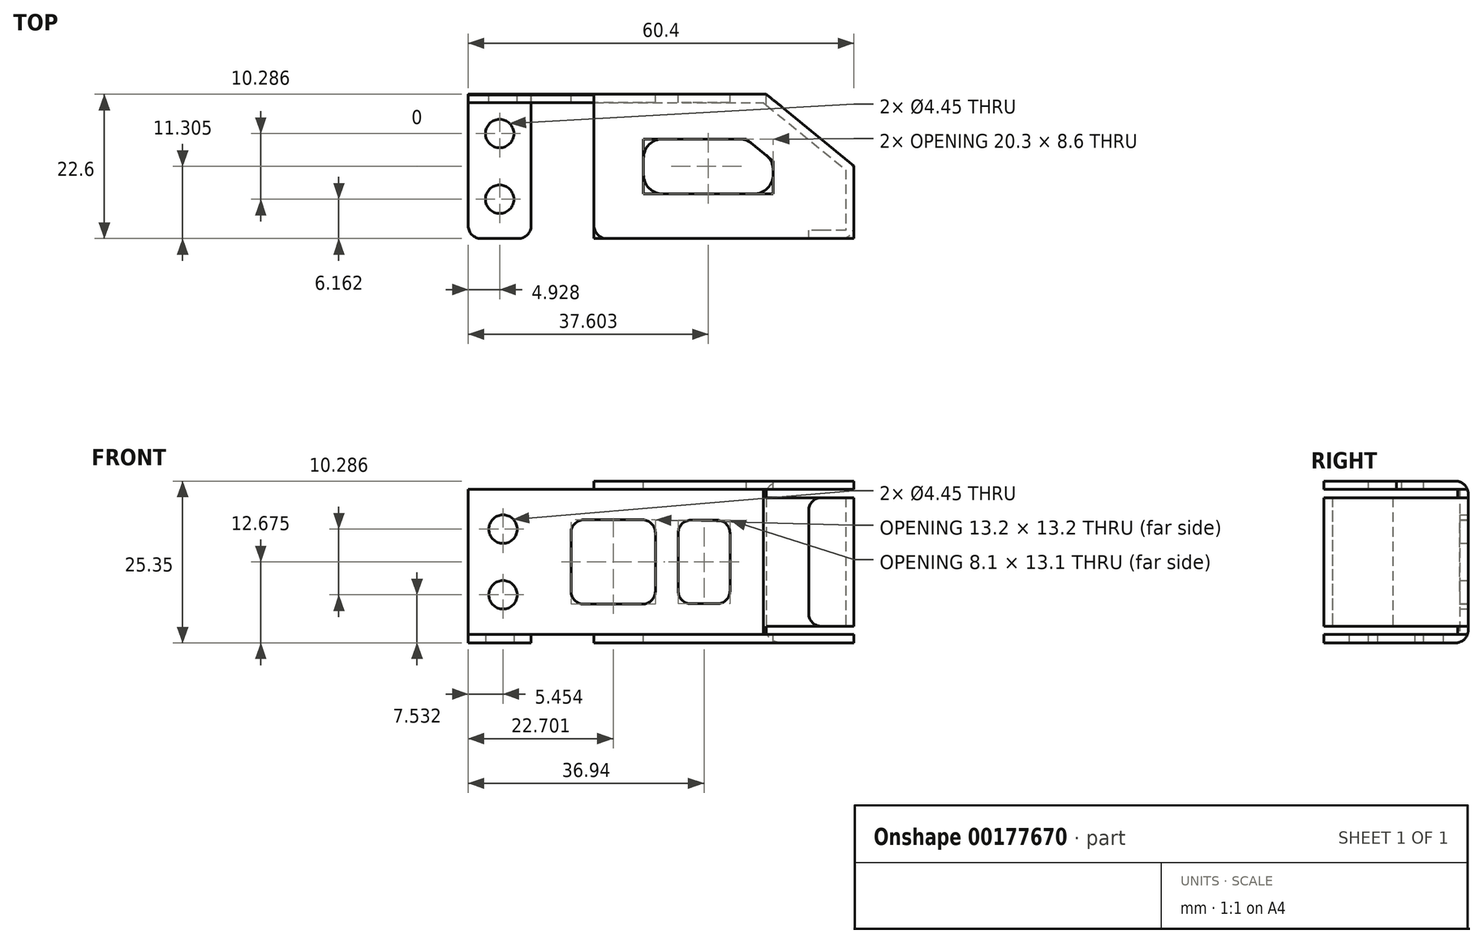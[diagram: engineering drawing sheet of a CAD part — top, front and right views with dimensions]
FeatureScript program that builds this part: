
annotation { "Feature Type Name" : "Feature", "Feature Type Description" : "" }
export const myFeature = defineFeature(function(context is Context, id is Id, definition is map)
    precondition{}
    {
        {
            var Q0;
            Q0=qCreatedBy(makeId("Top.planeOp"),FACE);
            var sketch = newSketch(context, id + "F0", { "sketchPlane" : qUnion([Q0])});
            skLineSegment(sketch, "E0.bottom", {"start": v(-31.59, -12.14) * mm, "end": v(13.31, -12.14) * mm});
            skLineSegment(sketch, "E0.top", {"start": v(-31.59, -33.44) * mm, "end": v(26.21, -33.44) * mm});
            skLineSegment(sketch, "E0.left", {"start": v(-31.59, -12.14) * mm, "end": v(-31.59, -33.44) * mm});
            skLineSegment(sketch, "E0.right", {"start": v(26.21, -22.66) * mm, "end": v(26.21, -33.44) * mm});
            skLineSegment(sketch, "E1", {"start": v(13.31, -12.14) * mm, "end": v(26.21, -22.66) * mm});
            skSolve(sketch);
        }
        {
            var Q0;
            Q0=makeQuery(id+"F0.imprint","IMPRINT",FACE,{"disambiguationData":[TD([[makeQuery(id+"F0.imprint","IMPRINT",EDGE,{"derivedFrom":sQuery(id+"F0.wireOp",EDGE,"E0.bottom")}),-1.0]])]});
            extrude(context, id + "F1", {"entities" : qUnion([Q0]), "depth" : 22.75 * mm});
        }
        {
            var Q0;
            Q0=makeQuery(id+"F1.opExtrude","SWEPT_FACE",FACE,{"disambiguationData":[OSD([sQuery(id+"F0.wireOp",EDGE,"E0.top")])]});
            shell(context, id + "F2", {"entities" : qUnion([Q0]), "thickness" : 1.3 * mm, "oppositeDirection" : true});
        }
        {
            var Q0;
            Q0=makeQuery(id+"F1.opExtrude","SWEPT_FACE",FACE,{"disambiguationData":[OSD([sQuery(id+"F0.wireOp",EDGE,"E0.left")])]});
            var sketch = newSketch(context, id + "F3", { "sketchPlane" : qUnion([Q0])});
            skLineSegment(sketch, "E2", {"start": v(12.14, -1.3) * mm, "end": v(12.14, 22.75) * mm});
            skLineSegment(sketch, "E3", {"start": v(12.14, 22.75) * mm, "end": v(33.44, 22.75) * mm});
            skSolve(sketch);
        }
        {
            var Q0;
            {var subQ0=sQuery(id+"F3.wireOp",EDGE,"E2");Q0=makeQuery(id+"F3.imprint","IMPRINT",FACE,{"disambiguationData":[TD([[makeQuery(id+"F3.imprint","IMPRINT",EDGE,{"derivedFrom":subQ0}),-1.0]])]});}
            extrude(context, id + "F4", {"entities" : qUnion([Q0]), "operationType" : NewBodyOperationType.REMOVE, "oppositeDirection" : true, "depth" : 19.7 * mm});
        }
        {
            var Q0;
            Q0=makeQuery(id+"F1.opExtrude","CAP_FACE",FACE,{"disambiguationData":[OSD([sQuery(id+"F0.wireOp",EDGE,"E0.bottom"),sQuery(id+"F0.wireOp",EDGE,"E0.top"),sQuery(id+"F0.wireOp",EDGE,"E0.left"),sQuery(id+"F0.wireOp",EDGE,"E0.right"),sQuery(id+"F0.wireOp",EDGE,"E1")])],"isStart":false});
            var sketch = newSketch(context, id + "F5", { "sketchPlane" : qUnion([Q0])});
            skLineSegment(sketch, "E4", {"start": v(-13.19, -12.14) * mm, "end": v(-13.19, -33.44) * mm});
            skLineSegment(sketch, "E5", {"start": v(-23.04, -33.44) * mm, "end": v(-23.04, -12.14) * mm});
            skLineSegment(sketch, "E6", {"start": v(-13.19, -33.44) * mm, "end": v(-32.89, -33.44) * mm});
            skLineSegment(sketch, "E7", {"start": v(-32.89, -33.44) * mm, "end": v(-23.04, -33.44) * mm});
            skLineSegment(sketch, "E8", {"start": v(-23.04, -12.14) * mm, "end": v(-32.89, -12.14) * mm});
            skLineSegment(sketch, "E9", {"start": v(-23.04, -12.14) * mm, "end": v(-23.04, -10.84) * mm});
            skLineSegment(sketch, "E10", {"start": v(-13.19, -12.14) * mm, "end": v(-13.19, -10.84) * mm});
            skSolve(sketch);
        }
        {
            var Q0;
            Q0=makeQuery(id+"F5.imprint","IMPRINT",FACE,{"disambiguationData":[TD([[makeQuery(id+"F5.imprint","IMPRINT",EDGE,{"derivedFrom":sQuery(id+"F5.wireOp",EDGE,"E4")}),-1.0]])]});
            extrude(context, id + "F6", {"entities" : qUnion([Q0]), "operationType" : NewBodyOperationType.REMOVE, "oppositeDirection" : true, "depth" : 1.3 * mm});
        }
        {
            var Q0;
            {var subQ0=sQuery(id+"F0.wireOp",EDGE,"E1");var subQ1=sQuery(id+"F0.wireOp",EDGE,"E0.top");var subQ2=sQuery(id+"F0.wireOp",EDGE,"E0.right");var subQ3=sQuery(id+"F0.wireOp",EDGE,"E0.bottom");Q0=makeQuery(id+"F6.boolean.opBoolean","SPLIT",FACE,{"disambiguationData":[TD([makeQuery(id+"F1.opExtrude","SWEPT_FACE",FACE,{"disambiguationData":[OSD([subQ2])]})])],"derivedFrom":makeQuery(id+"F1.opExtrude","CAP_FACE",FACE,{"disambiguationData":[OSD([subQ3,subQ1,sQuery(id+"F0.wireOp",EDGE,"E0.left"),subQ2,subQ0])],"isStart":false})});}
            var sketch = newSketch(context, id + "F7", { "sketchPlane" : qUnion([Q0])});
            skLineSegment(sketch, "E11", {"start": v(-5.44, -17.84) * mm, "end": v(10.65, -17.84) * mm});
            skLineSegment(sketch, "E12", {"start": v(10.65, -17.84) * mm, "end": v(14.86, -21.27) * mm});
            skLineSegment(sketch, "E13", {"start": v(14.86, -21.27) * mm, "end": v(14.86, -26.44) * mm});
            skLineSegment(sketch, "E14", {"start": v(14.86, -26.44) * mm, "end": v(-5.44, -26.44) * mm});
            skLineSegment(sketch, "E15", {"start": v(-5.44, -26.44) * mm, "end": v(-5.44, -17.84) * mm});
            skSolve(sketch);
        }
        {
            var Q0;
            Q0=makeQuery(id+"F7.imprint","IMPRINT",FACE,{"disambiguationData":[TD([[makeQuery(id+"F7.imprint","IMPRINT",EDGE,{"derivedFrom":sQuery(id+"F7.wireOp",EDGE,"E11")}),-1.0]])]});
            extrude(context, id + "F8", {"entities" : qUnion([Q0]), "operationType" : NewBodyOperationType.REMOVE, "oppositeDirection" : true, "depth" : 61.35 * mm});
        }
        {
            var Q0;
            Q0=makeQuery(id+"F1.opExtrude","SWEPT_FACE",FACE,{"disambiguationData":[OSD([sQuery(id+"F0.wireOp",EDGE,"E0.bottom")])]});
            var sketch = newSketch(context, id + "F9", { "sketchPlane" : qUnion([Q0])});
            skLineSegment(sketch, "E16.bottom", {"start": v(-8.1, 4.82) * mm, "end": v(0, 4.82) * mm});
            skLineSegment(sketch, "E16.top", {"start": v(-8.1, 17.93) * mm, "end": v(0, 17.93) * mm});
            skLineSegment(sketch, "E16.left", {"start": v(-8.1, 4.82) * mm, "end": v(-8.1, 17.93) * mm});
            skLineSegment(sketch, "E16.right", {"start": v(0, 4.82) * mm, "end": v(0, 17.93) * mm});
            skLineSegment(sketch, "E17.bottom", {"start": v(3.59, 4.77) * mm, "end": v(16.79, 4.77) * mm});
            skLineSegment(sketch, "E17.top", {"start": v(3.59, 17.97) * mm, "end": v(16.79, 17.97) * mm});
            skLineSegment(sketch, "E17.left", {"start": v(3.59, 4.77) * mm, "end": v(3.59, 17.98) * mm});
            skLineSegment(sketch, "E17.right", {"start": v(16.79, 4.77) * mm, "end": v(16.79, 17.97) * mm});
            skLineSegment(sketch, "E18", {"start": v(27.44, -1.3) * mm, "end": v(27.44, 24.05) * mm, "construction": true});
            skLineSegment(sketch, "E19", {"start": v(-13.78, 11.38) * mm, "end": v(32.89, 11.38) * mm, "construction": true});
            skCircle(sketch, "E20", {"center": v(27.44, 16.52) * mm, "radius": 2.23 * mm});
            skCircle(sketch, "E21", {"center": v(27.44, 6.23) * mm, "radius": 2.23 * mm});
            skLineSegment(sketch, "E22", {"start": v(27.44, 14.3) * mm, "end": v(27.44, 11.38) * mm});
            skLineSegment(sketch, "E23", {"start": v(27.44, 11.38) * mm, "end": v(27.44, 8.46) * mm});
            skLineSegment(sketch, "E24", {"start": v(13.19, -1.3) * mm, "end": v(13.19, 0) * mm});
            skLineSegment(sketch, "E25", {"start": v(13.19, 0) * mm, "end": v(32.89, 0) * mm});
            skPoint(sketch, "E26", {"position": v(16.79, 11.37) * mm});
            skPoint(sketch, "E27", {"position": v(0, 11.37) * mm});
            skSolve(sketch);
        }
        {
            var Q0;
            Q0=makeQuery(id+"F9.imprint","IMPRINT",FACE,{"disambiguationData":[TD([[makeQuery(id+"F9.imprint","IMPRINT",EDGE,{"derivedFrom":sQuery(id+"F9.wireOp",EDGE,"E16.bottom")}),1.0]])]});
            var Q1;
            Q1=makeQuery(id+"F9.imprint","IMPRINT",FACE,{"disambiguationData":[TD([[makeQuery(id+"F9.imprint","IMPRINT",EDGE,{"derivedFrom":sQuery(id+"F9.wireOp",EDGE,"E17.bottom")}),1.0]])]});
            var Q2;
            {var subQ0=sQuery(id+"F9.wireOp",EDGE,"E24");Q2=makeQuery(id+"F9.imprint","IMPRINT",FACE,{"disambiguationData":[TD([[makeQuery(id+"F9.imprint","IMPRINT",EDGE,{"derivedFrom":subQ0}),-1.0]])]});}
            var Q3;
            Q3=makeQuery(id+"F9.imprint","IMPRINT",FACE,{"disambiguationData":[TD([[makeQuery(id+"F9.imprint","IMPRINT",EDGE,{"derivedFrom":sQuery(id+"F9.wireOp",EDGE,"E21")}),1.0]])]});
            var Q4;
            Q4=makeQuery(id+"F9.imprint","IMPRINT",FACE,{"disambiguationData":[TD([[makeQuery(id+"F9.imprint","IMPRINT",EDGE,{"derivedFrom":sQuery(id+"F9.wireOp",EDGE,"E20")}),1.0]])]});
            extrude(context, id + "F10", {"entities" : qUnion([Q0, Q1, Q2, Q3, Q4]), "operationType" : NewBodyOperationType.REMOVE, "oppositeDirection" : true, "depth" : 25 * mm});
        }
        {
            var Q0;
            Q0=makeQuery(id+"F2.opShell","OFFSET_FACE",FACE,{"disambiguationData":[OSD([sQuery(id+"F0.wireOp",EDGE,"E0.right")])]});
            var sketch = newSketch(context, id + "F11", { "sketchPlane" : qUnion([Q0])});
            skLineSegment(sketch, "E28", {"start": v(32.14, 22.75) * mm, "end": v(32.14, 0) * mm});
            skSolve(sketch);
        }
        {
            var Q0;
            {var subQ0=sQuery(id+"F11.wireOp",EDGE,"E28");Q0=makeQuery(id+"F11.imprint","IMPRINT",FACE,{"disambiguationData":[TD([[makeQuery(id+"F11.imprint","IMPRINT",EDGE,{"derivedFrom":subQ0}),1.0]])]});}
            extrude(context, id + "F12", {"entities" : qUnion([Q0]), "operationType" : NewBodyOperationType.ADD, "depth" : 5.8 * mm});
        }
        {
            var Q0;
            Q0=makeQuery(id+"F1.opExtrude","SWEPT_FACE",FACE,{"disambiguationData":[OSD([sQuery(id+"F0.wireOp",EDGE,"E0.bottom")])]});
            var sketch = newSketch(context, id + "F13", { "sketchPlane" : qUnion([Q0])});
            skLineSegment(sketch, "E29", {"start": v(-13.78, 0) * mm, "end": v(-36.67, 0) * mm});
            skLineSegment(sketch, "E30", {"start": v(-13.78, 22.75) * mm, "end": v(-38.37, 22.75) * mm});
            skLineSegment(sketch, "E31", {"start": v(-13.78, 1.3) * mm, "end": v(-36.66, 1.3) * mm});
            skLineSegment(sketch, "E32", {"start": v(-13.78, 21.45) * mm, "end": v(-38.37, 21.45) * mm});
            skLineSegment(sketch, "E33", {"start": v(-36.67, 0) * mm, "end": v(-36.66, 1.3) * mm});
            skLineSegment(sketch, "E34", {"start": v(-38.37, 21.45) * mm, "end": v(-38.37, 22.75) * mm});
            skSolve(sketch);
        }
        {
            var Q0;
            {var subQ0=sQuery(id+"F13.wireOp",EDGE,"E29");Q0=makeQuery(id+"F13.imprint","IMPRINT",FACE,{"disambiguationData":[TD([[makeQuery(id+"F13.imprint","IMPRINT",EDGE,{"derivedFrom":subQ0}),-1.0]])]});}
            var Q1;
            {var subQ0=sQuery(id+"F13.wireOp",EDGE,"E30");Q1=makeQuery(id+"F13.imprint","IMPRINT",FACE,{"disambiguationData":[TD([[makeQuery(id+"F13.imprint","IMPRINT",EDGE,{"derivedFrom":subQ0}),1.0]])]});}
            extrude(context, id + "F14", {"entities" : qUnion([Q0, Q1]), "operationType" : NewBodyOperationType.REMOVE, "oppositeDirection" : true, "depth" : 25 * mm});
        }
        {
            var Q0;
            Q0=makeQuery(id+"F4.boolean.opBoolean","COPY",EDGE,{"derivedFrom":makeQuery(id+"F4.opExtrude","CAP_EDGE",EDGE,{"disambiguationData":[OSD([sQuery(id+"F0.wireOp",EDGE,"E0.top"),sQuery(id+"F0.wireOp",EDGE,"E0.left")])],"isStart":false})});
            var Q1;
            {var subQ0=sQuery(id+"F0.wireOp",EDGE,"E0.right");var subQ1=sQuery(id+"F0.wireOp",EDGE,"E0.top");Q1=makeQuery(id+"F14.boolean.opBoolean","SPLIT",EDGE,{"disambiguationData":[TD([makeQuery(id+"F14.opExtrude","SWEPT_FACE",FACE,{"disambiguationData":[OSD([sQuery(id+"F13.wireOp",EDGE,"E31")])]})])],"derivedFrom":makeQuery(id+"F1.opExtrude","SWEPT_EDGE",EDGE,{"disambiguationData":[OSD([subQ1,subQ0])]})});}
            var Q2;
            {var subQ1=sQuery(id+"F0.wireOp",EDGE,"E0.right");var subQ3=sQuery(id+"F0.wireOp",EDGE,"E0.top");Q2=makeQuery(id+"F14.boolean.opBoolean","SPLIT",EDGE,{"disambiguationData":[TD([makeQuery(id+"F14.opExtrude","SWEPT_FACE",FACE,{"disambiguationData":[OSD([sQuery(id+"F13.wireOp",EDGE,"E29")])]})])],"derivedFrom":makeQuery(id+"F1.opExtrude","SWEPT_EDGE",EDGE,{"disambiguationData":[OSD([subQ3,subQ1])]})});}
            var Q3;
            {var subQ1=sQuery(id+"F0.wireOp",EDGE,"E0.right");var subQ3=sQuery(id+"F0.wireOp",EDGE,"E0.top");Q3=makeQuery(id+"F14.boolean.opBoolean","SPLIT",EDGE,{"disambiguationData":[TD([makeQuery(id+"F4.opExtrude","SWEPT_FACE",FACE,{"disambiguationData":[OSD([sQuery(id+"F3.wireOp",EDGE,"E3")])]})])],"derivedFrom":makeQuery(id+"F1.opExtrude","SWEPT_EDGE",EDGE,{"disambiguationData":[OSD([subQ3,subQ1])]})});}
            var Q4;
            Q4=makeQuery(id+"F6.boolean.opBoolean","COPY",EDGE,{"derivedFrom":makeQuery(id+"F6.opExtrude","SWEPT_EDGE",EDGE,{"disambiguationData":[OSD([sQuery(id+"F0.wireOp",EDGE,"E0.top"),sQuery(id+"F5.wireOp",EDGE,"E4"),sQuery(id+"F5.wireOp",EDGE,"E6")])]})});
            var Q5;
            Q5=makeQuery(id+"F1.opExtrude","SWEPT_EDGE",EDGE,{"disambiguationData":[OSD([sQuery(id+"F0.wireOp",EDGE,"E0.top"),sQuery(id+"F0.wireOp",EDGE,"E0.left")])]});
            var Q6;
            Q6=makeQuery(id+"F6.boolean.opBoolean","COPY",EDGE,{"derivedFrom":makeQuery(id+"F6.opExtrude","SWEPT_EDGE",EDGE,{"disambiguationData":[OSD([sQuery(id+"F5.wireOp",EDGE,"E5"),sQuery(id+"F5.wireOp",EDGE,"E6"),sQuery(id+"F5.wireOp",EDGE,"E7")])]})});
            var Q7;
            Q7=makeQuery(id+"F10.boolean.opBoolean","COPY",EDGE,{"derivedFrom":makeQuery(id+"F10.opExtrude","SWEPT_EDGE",EDGE,{"disambiguationData":[OSD([sQuery(id+"F0.wireOp",EDGE,"E0.bottom"),sQuery(id+"F0.wireOp",EDGE,"E0.left"),sQuery(id+"F9.wireOp",EDGE,"E25")])]})});
            var Q8;
            Q8=makeQuery(id+"F14.boolean.opBoolean","INTERSECT",EDGE,{"derivedFrom":[makeQuery(id+"F12.opExtrude","CAP_FACE",FACE,{"disambiguationData":[OSD([sQuery(id+"F0.wireOp",EDGE,"E0.top"),sQuery(id+"F0.wireOp",EDGE,"E0.right"),sQuery(id+"F11.wireOp",EDGE,"E28")])],"isStart":false}),makeQuery(id+"F14.opExtrude","SWEPT_FACE",FACE,{"disambiguationData":[OSD([sQuery(id+"F13.wireOp",EDGE,"E31")])]})]});
            var Q9;
            Q9=makeQuery(id+"F14.boolean.opBoolean","INTERSECT",EDGE,{"derivedFrom":[makeQuery(id+"F12.opExtrude","CAP_FACE",FACE,{"disambiguationData":[OSD([sQuery(id+"F0.wireOp",EDGE,"E0.top"),sQuery(id+"F0.wireOp",EDGE,"E0.right"),sQuery(id+"F11.wireOp",EDGE,"E28")])],"isStart":false}),makeQuery(id+"F14.opExtrude","SWEPT_FACE",FACE,{"disambiguationData":[OSD([sQuery(id+"F13.wireOp",EDGE,"E32")])]})]});
            fillet(context, id + "F15", {"entities" : qUnion([Q0, Q1, Q2, Q3, Q4, Q5, Q6, Q7, Q8, Q9]), "radius" : 2 * mm, "tangentPropagation" : true, "allowEdgeOverflow" : false});
        }
        {
            var Q0;
            {var subQ0=sQuery(id+"F0.wireOp",EDGE,"E1");var subQ1=sQuery(id+"F0.wireOp",EDGE,"E0.right");var subQ2=sQuery(id+"F0.wireOp",EDGE,"E0.left");var subQ3=sQuery(id+"F0.wireOp",EDGE,"E0.top");var subQ4=sQuery(id+"F0.wireOp",EDGE,"E0.bottom");var subQ5=makeQuery(id+"F1.opExtrude","CAP_FACE",FACE,{"disambiguationData":[OSD([subQ4,subQ3,subQ2,subQ1,subQ0])],"isStart":true});var subQ6=sQuery(id+"F7.wireOp",EDGE,"E13");var subQ7=sQuery(id+"F7.wireOp",EDGE,"E12");Q0=makeQuery(id+"F8.boolean.opBoolean","COPY",EDGE,{"disambiguationData":[TD([subQ5])],"derivedFrom":makeQuery(id+"F8.opExtrude","SWEPT_EDGE",EDGE,{"disambiguationData":[OSD([subQ7,subQ6])]})});}
            var Q1;
            {var subQ0=sQuery(id+"F0.wireOp",EDGE,"E1");var subQ1=sQuery(id+"F0.wireOp",EDGE,"E0.right");var subQ2=sQuery(id+"F0.wireOp",EDGE,"E0.left");var subQ3=sQuery(id+"F0.wireOp",EDGE,"E0.top");var subQ4=sQuery(id+"F0.wireOp",EDGE,"E0.bottom");var subQ5=makeQuery(id+"F1.opExtrude","CAP_FACE",FACE,{"disambiguationData":[OSD([subQ4,subQ3,subQ2,subQ1,subQ0])],"isStart":true});var subQ6=sQuery(id+"F7.wireOp",EDGE,"E11");var subQ7=sQuery(id+"F7.wireOp",EDGE,"E12");Q1=makeQuery(id+"F8.boolean.opBoolean","COPY",EDGE,{"disambiguationData":[TD([subQ5])],"derivedFrom":makeQuery(id+"F8.opExtrude","SWEPT_EDGE",EDGE,{"disambiguationData":[OSD([subQ6,subQ7])]})});}
            var Q2;
            {var subQ0=sQuery(id+"F0.wireOp",EDGE,"E1");var subQ1=sQuery(id+"F0.wireOp",EDGE,"E0.right");var subQ2=sQuery(id+"F0.wireOp",EDGE,"E0.left");var subQ3=sQuery(id+"F0.wireOp",EDGE,"E0.top");var subQ4=sQuery(id+"F0.wireOp",EDGE,"E0.bottom");var subQ5=makeQuery(id+"F1.opExtrude","CAP_FACE",FACE,{"disambiguationData":[OSD([subQ4,subQ3,subQ2,subQ1,subQ0])],"isStart":true});var subQ6=sQuery(id+"F7.wireOp",EDGE,"E11");var subQ7=sQuery(id+"F7.wireOp",EDGE,"E15");Q2=makeQuery(id+"F8.boolean.opBoolean","COPY",EDGE,{"disambiguationData":[TD([subQ5])],"derivedFrom":makeQuery(id+"F8.opExtrude","SWEPT_EDGE",EDGE,{"disambiguationData":[OSD([subQ6,subQ7])]})});}
            var Q3;
            {var subQ0=sQuery(id+"F0.wireOp",EDGE,"E1");var subQ1=sQuery(id+"F0.wireOp",EDGE,"E0.right");var subQ2=sQuery(id+"F0.wireOp",EDGE,"E0.left");var subQ3=sQuery(id+"F0.wireOp",EDGE,"E0.top");var subQ4=sQuery(id+"F0.wireOp",EDGE,"E0.bottom");var subQ5=makeQuery(id+"F1.opExtrude","CAP_FACE",FACE,{"disambiguationData":[OSD([subQ4,subQ3,subQ2,subQ1,subQ0])],"isStart":true});var subQ6=sQuery(id+"F7.wireOp",EDGE,"E14");var subQ7=sQuery(id+"F7.wireOp",EDGE,"E15");Q3=makeQuery(id+"F8.boolean.opBoolean","COPY",EDGE,{"disambiguationData":[TD([subQ5])],"derivedFrom":makeQuery(id+"F8.opExtrude","SWEPT_EDGE",EDGE,{"disambiguationData":[OSD([subQ6,subQ7])]})});}
            var Q4;
            {var subQ0=sQuery(id+"F0.wireOp",EDGE,"E1");var subQ1=sQuery(id+"F0.wireOp",EDGE,"E0.right");var subQ2=sQuery(id+"F0.wireOp",EDGE,"E0.left");var subQ3=sQuery(id+"F0.wireOp",EDGE,"E0.top");var subQ4=sQuery(id+"F0.wireOp",EDGE,"E0.bottom");var subQ5=makeQuery(id+"F1.opExtrude","CAP_FACE",FACE,{"disambiguationData":[OSD([subQ4,subQ3,subQ2,subQ1,subQ0])],"isStart":true});var subQ6=sQuery(id+"F7.wireOp",EDGE,"E13");var subQ7=sQuery(id+"F7.wireOp",EDGE,"E14");Q4=makeQuery(id+"F8.boolean.opBoolean","COPY",EDGE,{"disambiguationData":[TD([subQ5])],"derivedFrom":makeQuery(id+"F8.opExtrude","SWEPT_EDGE",EDGE,{"disambiguationData":[OSD([subQ6,subQ7])]})});}
            var Q5;
            {var subQ0=sQuery(id+"F7.wireOp",EDGE,"E11");var subQ7=sQuery(id+"F7.wireOp",EDGE,"E12");Q5=makeQuery(id+"F8.boolean.opBoolean","COPY",EDGE,{"disambiguationData":[TD([makeQuery(id+"F4.opExtrude","SWEPT_FACE",FACE,{"disambiguationData":[OSD([sQuery(id+"F3.wireOp",EDGE,"E3")])]})])],"derivedFrom":makeQuery(id+"F8.opExtrude","SWEPT_EDGE",EDGE,{"disambiguationData":[OSD([subQ0,subQ7])]})});}
            var Q6;
            {var subQ0=sQuery(id+"F7.wireOp",EDGE,"E12");var subQ7=sQuery(id+"F7.wireOp",EDGE,"E13");Q6=makeQuery(id+"F8.boolean.opBoolean","COPY",EDGE,{"disambiguationData":[TD([makeQuery(id+"F4.opExtrude","SWEPT_FACE",FACE,{"disambiguationData":[OSD([sQuery(id+"F3.wireOp",EDGE,"E3")])]})])],"derivedFrom":makeQuery(id+"F8.opExtrude","SWEPT_EDGE",EDGE,{"disambiguationData":[OSD([subQ0,subQ7])]})});}
            var Q7;
            {var subQ0=sQuery(id+"F7.wireOp",EDGE,"E13");var subQ7=sQuery(id+"F7.wireOp",EDGE,"E14");Q7=makeQuery(id+"F8.boolean.opBoolean","COPY",EDGE,{"disambiguationData":[TD([makeQuery(id+"F4.opExtrude","SWEPT_FACE",FACE,{"disambiguationData":[OSD([sQuery(id+"F3.wireOp",EDGE,"E3")])]})])],"derivedFrom":makeQuery(id+"F8.opExtrude","SWEPT_EDGE",EDGE,{"disambiguationData":[OSD([subQ0,subQ7])]})});}
            var Q8;
            {var subQ0=sQuery(id+"F7.wireOp",EDGE,"E14");var subQ7=sQuery(id+"F7.wireOp",EDGE,"E15");Q8=makeQuery(id+"F8.boolean.opBoolean","COPY",EDGE,{"disambiguationData":[TD([makeQuery(id+"F4.opExtrude","SWEPT_FACE",FACE,{"disambiguationData":[OSD([sQuery(id+"F3.wireOp",EDGE,"E3")])]})])],"derivedFrom":makeQuery(id+"F8.opExtrude","SWEPT_EDGE",EDGE,{"disambiguationData":[OSD([subQ0,subQ7])]})});}
            var Q9;
            {var subQ0=sQuery(id+"F7.wireOp",EDGE,"E11");var subQ7=sQuery(id+"F7.wireOp",EDGE,"E15");Q9=makeQuery(id+"F8.boolean.opBoolean","COPY",EDGE,{"disambiguationData":[TD([makeQuery(id+"F4.opExtrude","SWEPT_FACE",FACE,{"disambiguationData":[OSD([sQuery(id+"F3.wireOp",EDGE,"E3")])]})])],"derivedFrom":makeQuery(id+"F8.opExtrude","SWEPT_EDGE",EDGE,{"disambiguationData":[OSD([subQ0,subQ7])]})});}
            fillet(context, id + "F16", {"entities" : qUnion([Q0, Q1, Q2, Q3, Q4, Q5, Q6, Q7, Q8, Q9]), "radius" : 3 * mm, "tangentPropagation" : true, "allowEdgeOverflow" : false});
        }
        {
            var Q0;
            {var subQ0=sQuery(id+"F0.wireOp",EDGE,"E0.bottom");var subQ1=sQuery(id+"F0.wireOp",EDGE,"E1");Q0=makeQuery(id+"F6.boolean.opBoolean","SPLIT",EDGE,{"disambiguationData":[TD([makeQuery(id+"F1.opExtrude","SWEPT_FACE",FACE,{"disambiguationData":[OSD([subQ1])]})])],"derivedFrom":makeQuery(id+"F1.opExtrude","CAP_EDGE",EDGE,{"disambiguationData":[OSD([subQ0])],"isStart":false})});}
            var Q1;
            {var subQ0=sQuery(id+"F0.wireOp",EDGE,"E0.bottom");var subQ1=sQuery(id+"F0.wireOp",EDGE,"E0.left");Q1=makeQuery(id+"F6.boolean.opBoolean","SPLIT",EDGE,{"disambiguationData":[TD([makeQuery(id+"F1.opExtrude","SWEPT_FACE",FACE,{"disambiguationData":[OSD([subQ1])]})])],"derivedFrom":makeQuery(id+"F1.opExtrude","CAP_EDGE",EDGE,{"disambiguationData":[OSD([subQ0])],"isStart":false})});}
            var Q2;
            Q2=makeQuery(id+"F1.opExtrude","CAP_EDGE",EDGE,{"disambiguationData":[OSD([sQuery(id+"F0.wireOp",EDGE,"E0.bottom")])],"isStart":true});
            var Q3;
            {var subQ0=sQuery(id+"F0.wireOp",EDGE,"E0.right");var subQ1=sQuery(id+"F0.wireOp",EDGE,"E1");Q3=makeQuery(id+"F14.boolean.opBoolean","SPLIT",EDGE,{"disambiguationData":[TD([makeQuery(id+"F14.opExtrude","SWEPT_FACE",FACE,{"disambiguationData":[OSD([sQuery(id+"F13.wireOp",EDGE,"E31")])]})])],"derivedFrom":makeQuery(id+"F1.opExtrude","SWEPT_EDGE",EDGE,{"disambiguationData":[OSD([subQ0,subQ1])]})});}
            var Q4;
            {var subQ0=sQuery(id+"F0.wireOp",EDGE,"E1");var subQ1=sQuery(id+"F0.wireOp",EDGE,"E0.right");Q4=makeQuery(id+"F14.boolean.opBoolean","SPLIT",EDGE,{"disambiguationData":[TD([makeQuery(id+"F4.opExtrude","SWEPT_FACE",FACE,{"disambiguationData":[OSD([sQuery(id+"F3.wireOp",EDGE,"E3")])]})])],"derivedFrom":makeQuery(id+"F1.opExtrude","SWEPT_EDGE",EDGE,{"disambiguationData":[OSD([subQ1,subQ0])]})});}
            var Q5;
            {var subQ0=sQuery(id+"F0.wireOp",EDGE,"E1");var subQ1=sQuery(id+"F0.wireOp",EDGE,"E0.right");Q5=makeQuery(id+"F14.boolean.opBoolean","SPLIT",EDGE,{"disambiguationData":[TD([makeQuery(id+"F14.opExtrude","SWEPT_FACE",FACE,{"disambiguationData":[OSD([sQuery(id+"F13.wireOp",EDGE,"E29")])]})])],"derivedFrom":makeQuery(id+"F1.opExtrude","SWEPT_EDGE",EDGE,{"disambiguationData":[OSD([subQ1,subQ0])]})});}
            fillet(context, id + "F17", {"entities" : qUnion([Q0, Q1, Q2, Q3, Q4, Q5]), "radius" : 2 * mm, "tangentPropagation" : true, "allowEdgeOverflow" : false});
        }
        {
            var Q0;
            Q0=makeQuery(id+"F10.boolean.opBoolean","COPY",EDGE,{"derivedFrom":makeQuery(id+"F10.opExtrude","SWEPT_EDGE",EDGE,{"disambiguationData":[OSD([sQuery(id+"F9.wireOp",EDGE,"E16.top"),sQuery(id+"F9.wireOp",EDGE,"E16.right")])]})});
            var Q1;
            Q1=makeQuery(id+"F10.boolean.opBoolean","COPY",EDGE,{"derivedFrom":makeQuery(id+"F10.opExtrude","SWEPT_EDGE",EDGE,{"disambiguationData":[OSD([sQuery(id+"F9.wireOp",EDGE,"E16.bottom"),sQuery(id+"F9.wireOp",EDGE,"E16.right")])]})});
            var Q2;
            Q2=makeQuery(id+"F10.boolean.opBoolean","COPY",EDGE,{"derivedFrom":makeQuery(id+"F10.opExtrude","SWEPT_EDGE",EDGE,{"disambiguationData":[OSD([sQuery(id+"F9.wireOp",EDGE,"E16.bottom"),sQuery(id+"F9.wireOp",EDGE,"E16.left")])]})});
            var Q3;
            Q3=makeQuery(id+"F10.boolean.opBoolean","COPY",EDGE,{"derivedFrom":makeQuery(id+"F10.opExtrude","SWEPT_EDGE",EDGE,{"disambiguationData":[OSD([sQuery(id+"F9.wireOp",EDGE,"E16.top"),sQuery(id+"F9.wireOp",EDGE,"E16.left")])]})});
            var Q4;
            Q4=makeQuery(id+"F10.boolean.opBoolean","COPY",EDGE,{"derivedFrom":makeQuery(id+"F10.opExtrude","SWEPT_EDGE",EDGE,{"disambiguationData":[OSD([sQuery(id+"F9.wireOp",EDGE,"E17.bottom"),sQuery(id+"F9.wireOp",EDGE,"E17.right")])]})});
            var Q5;
            Q5=makeQuery(id+"F10.boolean.opBoolean","COPY",EDGE,{"derivedFrom":makeQuery(id+"F10.opExtrude","SWEPT_EDGE",EDGE,{"disambiguationData":[OSD([sQuery(id+"F9.wireOp",EDGE,"E17.top"),sQuery(id+"F9.wireOp",EDGE,"E17.right")])]})});
            var Q6;
            Q6=makeQuery(id+"F10.boolean.opBoolean","COPY",EDGE,{"derivedFrom":makeQuery(id+"F10.opExtrude","SWEPT_EDGE",EDGE,{"disambiguationData":[OSD([sQuery(id+"F9.wireOp",EDGE,"E17.top"),sQuery(id+"F9.wireOp",EDGE,"E17.left")])]})});
            var Q7;
            Q7=makeQuery(id+"F10.boolean.opBoolean","COPY",EDGE,{"derivedFrom":makeQuery(id+"F10.opExtrude","SWEPT_EDGE",EDGE,{"disambiguationData":[OSD([sQuery(id+"F9.wireOp",EDGE,"E17.bottom"),sQuery(id+"F9.wireOp",EDGE,"E17.left")])]})});
            fillet(context, id + "F18", {"entities" : qUnion([Q0, Q1, Q2, Q3, Q4, Q5, Q6, Q7]), "radius" : 2 * mm, "tangentPropagation" : true, "allowEdgeOverflow" : false});
        }
        {
            var Q0;
            Q0=makeQuery(id+"F1.opExtrude","CAP_FACE",FACE,{"disambiguationData":[OSD([sQuery(id+"F0.wireOp",EDGE,"E0.bottom"),sQuery(id+"F0.wireOp",EDGE,"E0.top"),sQuery(id+"F0.wireOp",EDGE,"E0.left"),sQuery(id+"F0.wireOp",EDGE,"E0.right"),sQuery(id+"F0.wireOp",EDGE,"E1")])],"isStart":true});
            var sketch = newSketch(context, id + "F19", { "sketchPlane" : qUnion([Q0])});
            skLineSegment(sketch, "E35.0", {"start": v(13.78, 10.84) * mm, "end": v(-32.4, 10.84) * mm});
            skLineSegment(sketch, "E36.0", {"start": v(-23.04, 31.44) * mm, "end": v(-23.04, 12.14) * mm});
            skArc(sketch, "E37.0", {"start": v(-23.04, 31.44) * mm, "mid": v(-23.62, 32.85) * mm, "end": v(-25.04, 33.44) * mm});
            skLineSegment(sketch, "E38.0", {"start": v(-30.89, 33.44) * mm, "end": v(-25.04, 33.44) * mm});
            skArc(sketch, "E39.0", {"start": v(-30.89, 33.44) * mm, "mid": v(-32.3, 32.85) * mm, "end": v(-32.89, 31.44) * mm});
            skLineSegment(sketch, "E40.0", {"start": v(-32.89, 12.14) * mm, "end": v(-32.89, 31.44) * mm});
            skLineSegment(sketch, "E41", {"start": v(-23.04, 12.14) * mm, "end": v(-23.04, 10.84) * mm});
            skLineSegment(sketch, "E42", {"start": v(-23.04, 10.84) * mm, "end": v(-32.89, 10.84) * mm});
            skLineSegment(sketch, "E43", {"start": v(-32.89, 10.84) * mm, "end": v(-32.89, 12.14) * mm});
            skSolve(sketch);
        }
        {
            var Q0;
            Q0=qSketchRegion(id+"F19",true);
            extrude(context, id + "F20", {"entities" : qUnion([Q0]), "operationType" : NewBodyOperationType.ADD, "oppositeDirection" : true, "depth" : 1.3 * mm});
        }
        {
            var Q0;
            Q0=makeQuery(id+"F20.opExtrude","CAP_FACE",FACE,{"disambiguationData":[OSD([sQuery(id+"F19.wireOp",EDGE,"E36.0"),sQuery(id+"F19.wireOp",EDGE,"E37.0"),sQuery(id+"F19.wireOp",EDGE,"E38.0"),sQuery(id+"F19.wireOp",EDGE,"E39.0"),sQuery(id+"F19.wireOp",EDGE,"E40.0"),sQuery(id+"F19.wireOp",EDGE,"E41"),sQuery(id+"F19.wireOp",EDGE,"E42"),sQuery(id+"F19.wireOp",EDGE,"E43")])],"isStart":false});
            var sketch = newSketch(context, id + "F21", { "sketchPlane" : qUnion([Q0])});
            skLineSegment(sketch, "E44.0", {"start": v(-32.89, -10.84) * mm, "end": v(-32.89, -12.14) * mm});
            skLineSegment(sketch, "E45.0", {"start": v(-23.04, -12.14) * mm, "end": v(-30.89, -12.14) * mm});
            skLineSegment(sketch, "E46", {"start": v(-30.89, -12.14) * mm, "end": v(-32.89, -12.14) * mm});
            skLineSegment(sketch, "E47", {"start": v(-23.04, -12.14) * mm, "end": v(-23.04, -10.96) * mm});
            skLineSegment(sketch, "E48", {"start": v(-23.04, -10.96) * mm, "end": v(-23.04, -10.84) * mm});
            skLineSegment(sketch, "E49", {"start": v(-23.04, -10.84) * mm, "end": v(-32.89, -10.84) * mm});
            skSolve(sketch);
        }
        {
            var Q0;
            Q0=qSketchRegion(id+"F21",true);
            extrude(context, id + "F22", {"entities" : qUnion([Q0]), "operationType" : NewBodyOperationType.ADD, "depth" : 2.5 * mm});
        }
        {
            var Q0;
            Q0=makeQuery(id+"F20.opExtrude","CAP_EDGE",EDGE,{"disambiguationData":[OSD([sQuery(id+"F19.wireOp",EDGE,"E42")])],"isStart":true});
            fillet(context, id + "F23", {"entities" : qUnion([Q0]), "radius" : 2 * mm, "tangentPropagation" : true, "allowEdgeOverflow" : false});
        }
        {
            var Q0;
            {var subQ0=sQuery(id+"F0.wireOp",EDGE,"E0.bottom");var subQ1=sQuery(id+"F0.wireOp",EDGE,"E0.top");var subQ2=sQuery(id+"F0.wireOp",EDGE,"E0.left");Q0=makeQuery(id+"F6.boolean.opBoolean","SPLIT",FACE,{"disambiguationData":[TD([makeQuery(id+"F1.opExtrude","SWEPT_FACE",FACE,{"disambiguationData":[OSD([subQ2])]})])],"derivedFrom":makeQuery(id+"F1.opExtrude","CAP_FACE",FACE,{"disambiguationData":[OSD([subQ0,subQ1,subQ2,sQuery(id+"F0.wireOp",EDGE,"E0.right"),sQuery(id+"F0.wireOp",EDGE,"E1")])],"isStart":false})});}
            var sketch = newSketch(context, id + "F24", { "sketchPlane" : qUnion([Q0])});
            skLineSegment(sketch, "E50.0", {"start": v(-13.19, -10.96) * mm, "end": v(-13.19, -12.14) * mm});
            skLineSegment(sketch, "E51.0", {"start": v(-32.89, -10.84) * mm, "end": v(-13.19, -10.84) * mm});
            skLineSegment(sketch, "E52.0", {"start": v(-32.89, -12.84) * mm, "end": v(-32.89, -31.44) * mm});
            skLineSegment(sketch, "E53.0", {"start": v(-32.89, -12.84) * mm, "end": v(-32.89, -10.84) * mm});
            skLineSegment(sketch, "E54.0", {"start": v(-13.19, -12.84) * mm, "end": v(-13.19, -10.96) * mm});
            skLineSegment(sketch, "E55.0", {"start": v(-13.19, -12.84) * mm, "end": v(-13.19, -31.44) * mm});
            skLineSegment(sketch, "E56.0", {"start": v(-30.89, -33.44) * mm, "end": v(-25.04, -33.44) * mm});
            skArc(sketch, "E57.0", {"start": v(-32.89, -31.44) * mm, "mid": v(-32.3, -32.85) * mm, "end": v(-30.89, -33.44) * mm});
            skLineSegment(sketch, "E58", {"start": v(-13.19, -33.44) * mm, "end": v(-25.04, -33.44) * mm});
            skLineSegment(sketch, "E59", {"start": v(-13.19, -31.44) * mm, "end": v(-13.19, -33.44) * mm});
            skPoint(sketch, "E60.orphan", {"position": v(-11.19, -33.44) * mm});
            skLineSegment(sketch, "E61", {"start": v(-13.19, -10.96) * mm, "end": v(-13.19, -10.84) * mm});
            skPoint(sketch, "E62.orphan", {"position": v(13.78, -10.84) * mm});
            skSolve(sketch);
        }
        {
            var Q0;
            Q0=qSketchRegion(id+"F24",true);
            extrude(context, id + "F25", {"entities" : qUnion([Q0]), "operationType" : NewBodyOperationType.REMOVE, "oppositeDirection" : true, "depth" : 1.3 * mm});
        }
        {
            var Q0;
            Q0=makeQuery(id+"F20.opExtrude","CAP_FACE",FACE,{"disambiguationData":[OSD([sQuery(id+"F19.wireOp",EDGE,"E36.0"),sQuery(id+"F19.wireOp",EDGE,"E37.0"),sQuery(id+"F19.wireOp",EDGE,"E38.0"),sQuery(id+"F19.wireOp",EDGE,"E39.0"),sQuery(id+"F19.wireOp",EDGE,"E40.0"),sQuery(id+"F19.wireOp",EDGE,"E41"),sQuery(id+"F19.wireOp",EDGE,"E42"),sQuery(id+"F19.wireOp",EDGE,"E43")])],"isStart":true});
            var sketch = newSketch(context, id + "F26", { "sketchPlane" : qUnion([Q0])});
            skLineSegment(sketch, "E63", {"start": v(-23.04, 22.14) * mm, "end": v(-32.89, 22.14) * mm, "construction": true});
            skLineSegment(sketch, "E64", {"start": v(-27.96, 12.84) * mm, "end": v(-27.96, 33.44) * mm, "construction": true});
            skCircle(sketch, "E65", {"center": v(-27.96, 27.28) * mm, "radius": 2.23 * mm});
            skCircle(sketch, "E66", {"center": v(-27.96, 17) * mm, "radius": 2.23 * mm});
            skLineSegment(sketch, "E67", {"start": v(-27.96, 17) * mm, "end": v(-27.96, 27.28) * mm, "construction": true});
            skPoint(sketch, "E68", {"position": v(-27.96, 22.14) * mm});
            skSolve(sketch);
        }
        {
            var Q0;
            Q0=qSketchRegion(id+"F26",true);
            extrude(context, id + "F27", {"entities" : qUnion([Q0]), "operationType" : NewBodyOperationType.REMOVE, "oppositeDirection" : true, "depth" : 25 * mm});
        }
    });
